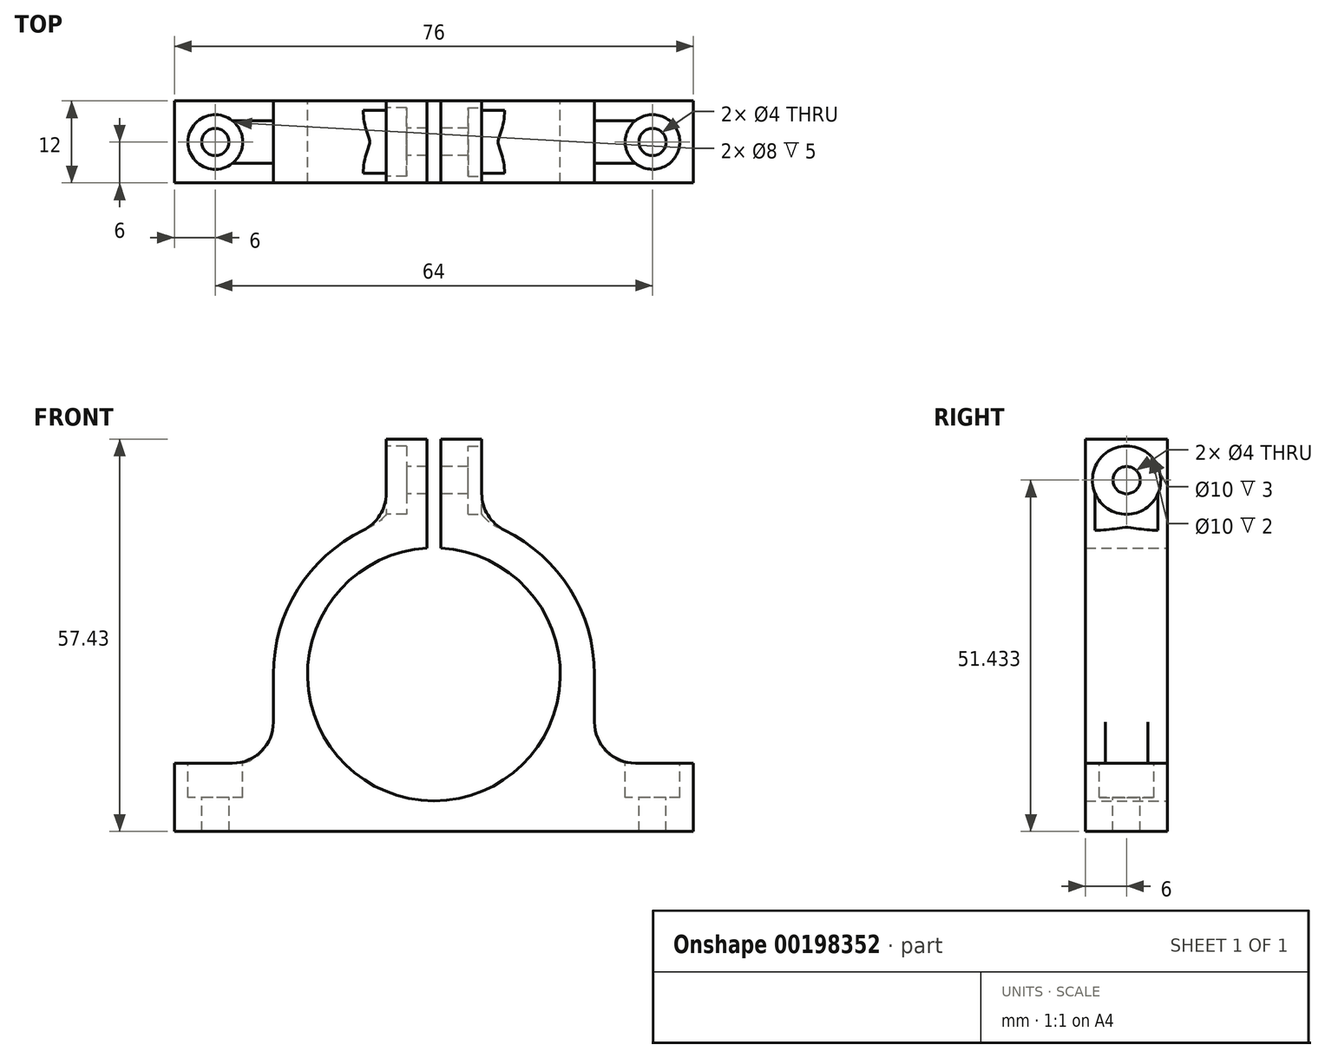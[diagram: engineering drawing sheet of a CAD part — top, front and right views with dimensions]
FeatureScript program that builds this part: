
annotation { "Feature Type Name" : "Feature", "Feature Type Description" : "" }
export const myFeature = defineFeature(function(context is Context, id is Id, definition is map)
    precondition{}
    {
        {
            var Q0;
            Q0=qCreatedBy(makeId("Front.planeOp"),FACE);
            var sketch = newSketch(context, id + "F0", { "sketchPlane" : qUnion([Q0])});
            skArc(sketch, "E0", {"start": v(-1, 18.47) * mm, "mid": v(0, -18.5) * mm, "end": v(1, 18.47) * mm});
            skLineSegment(sketch, "E1", {"start": v(-38, -23) * mm, "end": v(38, -23) * mm});
            skLineSegment(sketch, "E2", {"start": v(38, -23) * mm, "end": v(38, -13) * mm});
            skLineSegment(sketch, "E3", {"start": v(38, -13) * mm, "end": v(23.5, -13) * mm});
            skLineSegment(sketch, "E4", {"start": v(23.5, -13) * mm, "end": v(23.5, 0) * mm});
            skLineSegment(sketch, "E5", {"start": v(-38, -23) * mm, "end": v(-38, -13) * mm});
            skLineSegment(sketch, "E6", {"start": v(-38, -13) * mm, "end": v(-23.5, -13) * mm});
            skLineSegment(sketch, "E7", {"start": v(-23.5, -13) * mm, "end": v(-23.5, 0) * mm});
            skArc(sketch, "E8", {"start": v(-23.5, 0) * mm, "mid": v(-18.93, 13.92) * mm, "end": v(-7, 22.43) * mm});
            skPoint(sketch, "E9.visualSharp", {"position": v(-23.5, -13) * mm});
            skPoint(sketch, "E10.visualSharp", {"position": v(23.5, -13) * mm});
            skLineSegment(sketch, "E11", {"start": v(-1, 18.47) * mm, "end": v(-1, 34.43) * mm});
            skLineSegment(sketch, "E12", {"start": v(-1, 34.43) * mm, "end": v(-7, 34.43) * mm});
            skLineSegment(sketch, "E13", {"start": v(-7, 34.43) * mm, "end": v(-7, 22.43) * mm});
            skLineSegment(sketch, "E14", {"start": v(1, 18.47) * mm, "end": v(1, 34.43) * mm});
            skLineSegment(sketch, "E15", {"start": v(1, 34.43) * mm, "end": v(7, 34.43) * mm});
            skLineSegment(sketch, "E16", {"start": v(7, 34.43) * mm, "end": v(7, 22.43) * mm});
            skArc(sketch, "E17.trimOffspring", {"start": v(7, 22.43) * mm, "mid": v(18.93, 13.92) * mm, "end": v(23.5, 0) * mm});
            skSolve(sketch);
        }
        {
            var Q0;
            Q0=makeQuery(id+"F0.imprint","IMPRINT",FACE,{"disambiguationData":[TD([[makeQuery(id+"F0.imprint","IMPRINT",EDGE,{"derivedFrom":sQuery(id+"F0.wireOp",EDGE,"E0")}),-1.0]])]});
            extrude(context, id + "F1", {"entities" : qUnion([Q0]), "endBound" : BoundingType.SYMMETRIC, "depth" : 12 * mm});
        }
        {
            var Q0;
            Q0=makeQuery(id+"F1.opExtrude","SWEPT_FACE",FACE,{"disambiguationData":[OSD([sQuery(id+"F0.wireOp",EDGE,"E6")])]});
            var sketch = newSketch(context, id + "F2", { "sketchPlane" : qUnion([Q0])});
            skPoint(sketch, "E18", {"position": v(32, 0) * mm});
            skPoint(sketch, "E19", {"position": v(-32, 0) * mm});
            skPoint(sketch, "E20", {"position": v(-38, 0) * mm});
            skSolve(sketch);
        }
        {
            var Q0;
            Q0=sQuery(id+"F2.wireOp",VERTEX,"E18");
            var Q1;
            Q1=sQuery(id+"F2.wireOp",VERTEX,"E19");
            var Q2;
            Q2=makeQuery(id+"F1.opExtrude","SWEPT_BODY",BODY,{"disambiguationData":[OSD([sQuery(id+"F0.wireOp",EDGE,"E0"),sQuery(id+"F0.wireOp",EDGE,"E1"),sQuery(id+"F0.wireOp",EDGE,"E2"),sQuery(id+"F0.wireOp",EDGE,"E3"),sQuery(id+"F0.wireOp",EDGE,"E4"),sQuery(id+"F0.wireOp",EDGE,"E5"),sQuery(id+"F0.wireOp",EDGE,"E6"),sQuery(id+"F0.wireOp",EDGE,"E7"),sQuery(id+"F0.wireOp",EDGE,"E8"),sQuery(id+"F0.wireOp",EDGE,"E9.filletArc"),sQuery(id+"F0.wireOp",EDGE,"E10.filletArc"),sQuery(id+"F0.wireOp",EDGE,"E11"),sQuery(id+"F0.wireOp",EDGE,"E12"),sQuery(id+"F0.wireOp",EDGE,"E13"),sQuery(id+"F0.wireOp",EDGE,"E14"),sQuery(id+"F0.wireOp",EDGE,"E15"),sQuery(id+"F0.wireOp",EDGE,"E16"),sQuery(id+"F0.wireOp",EDGE,"E17.trimOffspring")])]});
            hole(context, id + "F6", {"style" : HoleStyle.C_BORE, "endStyle" : HoleEndStyle.THROUGH, "standardTappedOrClearance" : lookupTablePath({ "standard" : "ANSI", "size" : "#6" }), "standardBlindInLast" : lookupTablePath({ "standard" : "ANSI", "size" : "#6" }), "holeDiameter" : 4 * mm, "cBoreDiameter" : 8 * mm, "cBoreDepth" : 5 * mm, "locations" : qUnion([Q0, Q1]), "scope" : qUnion([Q2]), "isTappedThrough" : true});
        }
        {
            var Q0;
            Q0=makeQuery(id+"F1.opExtrude","SWEPT_FACE",FACE,{"disambiguationData":[OSD([sQuery(id+"F0.wireOp",EDGE,"E13")])]});
            var sketch = newSketch(context, id + "F3", { "sketchPlane" : qUnion([Q0])});
            skPoint(sketch, "E21", {"position": v(0, 28.43) * mm});
            skPoint(sketch, "E22", {"position": v(-6, 28.43) * mm});
            skPoint(sketch, "E23", {"position": v(0, 34.43) * mm});
            skSolve(sketch);
        }
        {
            var Q0;
            Q0=sQuery(id+"F3.wireOp",VERTEX,"E21");
            var Q1;
            Q1=makeQuery(id+"F1.opExtrude","SWEPT_BODY",BODY,{"disambiguationData":[OSD([sQuery(id+"F0.wireOp",EDGE,"E0"),sQuery(id+"F0.wireOp",EDGE,"E1"),sQuery(id+"F0.wireOp",EDGE,"E2"),sQuery(id+"F0.wireOp",EDGE,"E3"),sQuery(id+"F0.wireOp",EDGE,"E4"),sQuery(id+"F0.wireOp",EDGE,"E5"),sQuery(id+"F0.wireOp",EDGE,"E6"),sQuery(id+"F0.wireOp",EDGE,"E7"),sQuery(id+"F0.wireOp",EDGE,"E8"),sQuery(id+"F0.wireOp",EDGE,"E11"),sQuery(id+"F0.wireOp",EDGE,"E12"),sQuery(id+"F0.wireOp",EDGE,"E13"),sQuery(id+"F0.wireOp",EDGE,"E14"),sQuery(id+"F0.wireOp",EDGE,"E15"),sQuery(id+"F0.wireOp",EDGE,"E16"),sQuery(id+"F0.wireOp",EDGE,"E17.trimOffspring")])]});
            hole(context, id + "F4", {"style" : HoleStyle.C_BORE, "endStyle" : HoleEndStyle.THROUGH, "holeDiameter" : 4 * mm, "cBoreDiameter" : 10 * mm, "cBoreDepth" : 3 * mm, "locations" : qUnion([Q0]), "scope" : qUnion([Q1]), "isTappedThrough" : true});
        }
        {
            var Q0;
            Q0=makeQuery(id+"F1.opExtrude","SWEPT_FACE",FACE,{"disambiguationData":[OSD([sQuery(id+"F0.wireOp",EDGE,"E16")])]});
            var sketch = newSketch(context, id + "F7", { "sketchPlane" : qUnion([Q0])});
            skPoint(sketch, "E24", {"position": v(0, 28.43) * mm});
            skSolve(sketch);
        }
        {
            var Q0;
            Q0=sQuery(id+"F7.wireOp",VERTEX,"E24");
            var Q1;
            Q1=makeQuery(id+"F1.opExtrude","SWEPT_BODY",BODY,{"disambiguationData":[OSD([sQuery(id+"F0.wireOp",EDGE,"E0"),sQuery(id+"F0.wireOp",EDGE,"E1"),sQuery(id+"F0.wireOp",EDGE,"E2"),sQuery(id+"F0.wireOp",EDGE,"E3"),sQuery(id+"F0.wireOp",EDGE,"E4"),sQuery(id+"F0.wireOp",EDGE,"E5"),sQuery(id+"F0.wireOp",EDGE,"E6"),sQuery(id+"F0.wireOp",EDGE,"E7"),sQuery(id+"F0.wireOp",EDGE,"E8"),sQuery(id+"F0.wireOp",EDGE,"E11"),sQuery(id+"F0.wireOp",EDGE,"E12"),sQuery(id+"F0.wireOp",EDGE,"E13"),sQuery(id+"F0.wireOp",EDGE,"E14"),sQuery(id+"F0.wireOp",EDGE,"E15"),sQuery(id+"F0.wireOp",EDGE,"E16"),sQuery(id+"F0.wireOp",EDGE,"E17.trimOffspring")])]});
            hole(context, id + "F5", {"style" : HoleStyle.C_BORE, "endStyle" : HoleEndStyle.THROUGH, "holeDiameter" : 4 * mm, "cBoreDiameter" : 10 * mm, "cBoreDepth" : 2 * mm, "locations" : qUnion([Q0]), "scope" : qUnion([Q1]), "isTappedThrough" : true});
        }
        {
            var Q0;
            Q0=makeQuery(id+"F1.opExtrude","SWEPT_EDGE",EDGE,{"disambiguationData":[OSD([sQuery(id+"F0.wireOp",EDGE,"E16"),sQuery(id+"F0.wireOp",EDGE,"E17.trimOffspring")])]});
            var Q1;
            Q1=makeQuery(id+"F1.opExtrude","SWEPT_EDGE",EDGE,{"disambiguationData":[OSD([sQuery(id+"F0.wireOp",EDGE,"E3"),sQuery(id+"F0.wireOp",EDGE,"E4")])]});
            var Q2;
            Q2=makeQuery(id+"F1.opExtrude","SWEPT_EDGE",EDGE,{"disambiguationData":[OSD([sQuery(id+"F0.wireOp",EDGE,"E8"),sQuery(id+"F0.wireOp",EDGE,"E13")])]});
            var Q3;
            Q3=makeQuery(id+"F1.opExtrude","SWEPT_EDGE",EDGE,{"disambiguationData":[OSD([sQuery(id+"F0.wireOp",EDGE,"E6"),sQuery(id+"F0.wireOp",EDGE,"E7")])]});
            fillet(context, id + "F8", {"entities" : qUnion([Q0, Q1, Q2, Q3]), "radius" : 6 * mm, "tangentPropagation" : true, "allowEdgeOverflow" : false});
        }
    });
